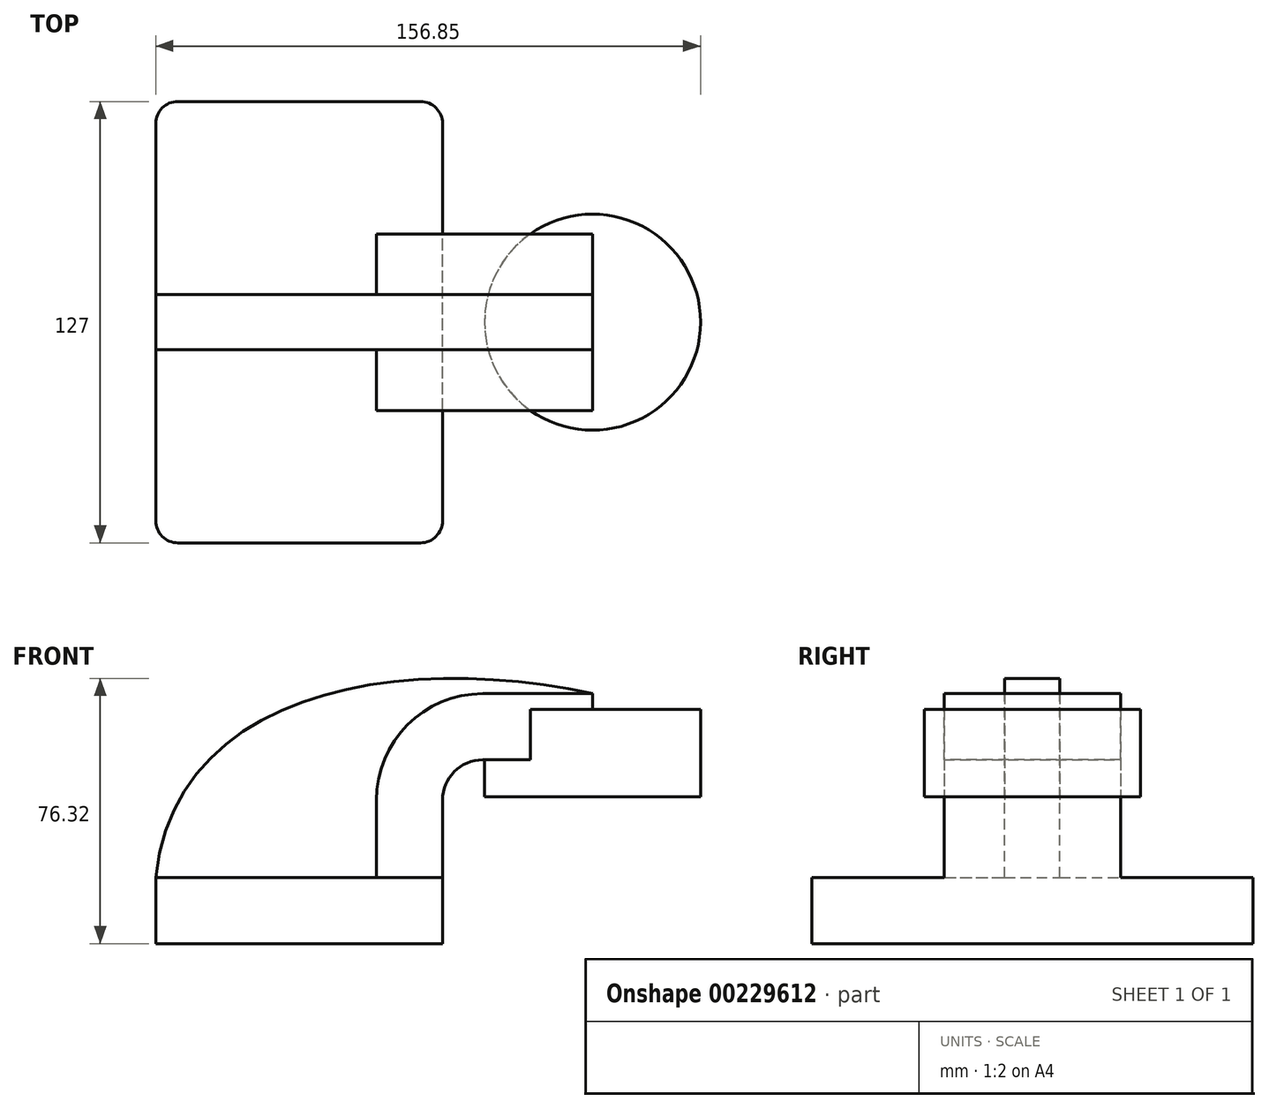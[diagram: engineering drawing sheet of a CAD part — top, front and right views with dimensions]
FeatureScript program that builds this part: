
annotation { "Feature Type Name" : "Feature", "Feature Type Description" : "" }
export const myFeature = defineFeature(function(context is Context, id is Id, definition is map)
    precondition{}
    {
        {
            var Q0;
            Q0=qCreatedBy(makeId("Front.planeOp"),FACE);
            var sketch = newSketch(context, id + "F0", { "sketchPlane" : qUnion([Q0])});
            skLineSegment(sketch, "E0.bottom", {"start": v(-41.28, -9.53) * mm, "end": v(41.28, -9.53) * mm});
            skLineSegment(sketch, "E0.top", {"start": v(-41.28, 9.52) * mm, "end": v(41.28, 9.52) * mm});
            skLineSegment(sketch, "E0.left", {"start": v(-41.28, -9.53) * mm, "end": v(-41.28, 9.53) * mm});
            skLineSegment(sketch, "E0.right", {"start": v(41.28, -9.53) * mm, "end": v(41.28, 9.52) * mm});
            skPoint(sketch, "E0.middle", {"position": v(0, 0) * mm});
            skLineSegment(sketch, "E1.bottom", {"start": v(64.77, 32.69) * mm, "end": v(115.57, 32.69) * mm});
            skLineSegment(sketch, "E1.top", {"start": v(64.77, 57.83) * mm, "end": v(115.57, 57.83) * mm});
            skLineSegment(sketch, "E1.left", {"start": v(64.77, 32.69) * mm, "end": v(64.77, 57.83) * mm});
            skLineSegment(sketch, "E1.right", {"start": v(115.57, 32.69) * mm, "end": v(115.57, 57.83) * mm});
            skPoint(sketch, "E1.middle", {"position": v(90.17, 45.26) * mm});
            skLineSegment(sketch, "E2", {"start": v(41.28, 9.52) * mm, "end": v(41.28, 31.75) * mm});
            skArc(sketch, "E3", {"start": v(41.27, 31.75) * mm, "mid": v(44.67, 39.94) * mm, "end": v(52.86, 43.33) * mm});
            skLineSegment(sketch, "E4", {"start": v(52.86, 43.33) * mm, "end": v(84.48, 43.33) * mm});
            skLineSegment(sketch, "E5.0", {"start": v(52.86, 62.38) * mm, "end": v(84.48, 62.38) * mm});
            skArc(sketch, "E5.1", {"start": v(22.22, 31.75) * mm, "mid": v(31.2, 53.41) * mm, "end": v(52.86, 62.38) * mm});
            skLineSegment(sketch, "E5.2", {"start": v(22.22, 9.52) * mm, "end": v(22.22, 31.75) * mm});
            skLineSegment(sketch, "E6", {"start": v(84.48, 62.38) * mm, "end": v(84.48, 32.69) * mm});
            skFitSpline(sketch, "E7", {"points": [v(-41.28, 9.52) * mm, v(84.48, 62.38) * mm], "startDerivative": vector(17.59, 165.45) * mm, "endDerivative": vector(159, -34.92) * mm});
            skSolve(sketch);
        }
        {
            var Q0;
            Q0=makeQuery(id+"F0.imprint","IMPRINT",FACE,{"disambiguationData":[TD([[makeQuery(id+"F0.imprint","IMPRINT",EDGE,{"derivedFrom":sQuery(id+"F0.wireOp",EDGE,"E0.bottom")}),1.0]])]});
            extrude(context, id + "F1", {"entities" : qUnion([Q0]), "depth" : 127 * mm, "symmetric" : true});
        }
        {
            var Q0;
            {var subQ0=sQuery(id+"F0.wireOp",EDGE,"E2");Q0=makeQuery(id+"F0.imprint","IMPRINT",FACE,{"disambiguationData":[TD([[makeQuery(id+"F0.imprint","IMPRINT",EDGE,{"derivedFrom":subQ0}),1.0]])]});}
            var Q1;
            {var subQ0=sQuery(id+"F0.wireOp",EDGE,"E1.left");var subQ1=sQuery(id+"F0.wireOp",EDGE,"E1.top");var subQ2=makeQuery(id+"F0.imprint","INTERSECT",VERTEX,{"derivedFrom":[subQ1,subQ0]});Q1=makeQuery(id+"F0.imprint","IMPRINT",FACE,{"disambiguationData":[TD([[makeQuery(id+"F0.imprint","IMPRINT",EDGE,{"disambiguationData":[TD([[subQ2,-1.0]])],"derivedFrom":subQ1}),-1.0]])]});}
            extrude(context, id + "F2", {"entities" : qUnion([Q0, Q1]), "operationType" : NewBodyOperationType.ADD, "depth" : 50.8 * mm, "symmetric" : true});
        }
        {
            var Q0;
            Q0=makeQuery(id+"F0.imprint","IMPRINT",FACE,{"disambiguationData":[TD([[makeQuery(id+"F0.imprint","IMPRINT",EDGE,{"derivedFrom":sQuery(id+"F0.wireOp",EDGE,"E5.0")}),1.0]])]});
            extrude(context, id + "F3", {"entities" : qUnion([Q0]), "operationType" : NewBodyOperationType.ADD, "depth" : 15.88 * mm, "symmetric" : true});
        }
        {
            var Q0;
            {var subQ0=sQuery(id+"F0.wireOp",EDGE,"E1.right");Q0=makeQuery(id+"F0.imprint","IMPRINT",FACE,{"disambiguationData":[TD([[makeQuery(id+"F0.imprint","IMPRINT",EDGE,{"derivedFrom":subQ0}),1.0]])]});}
            var Q1;
            Q1=sQuery(id+"F0.wireOp",EDGE,"E6");
            revolve(context, id + "F4", {"operationType" : NewBodyOperationType.ADD, "entities" : qUnion([Q0]), "axis" : qUnion([Q1]), "revolveType" : RevolveType.FULL});
        }
        {
            var Q0;
            Q0=makeQuery(id+"F1.opExtrude","CAP_EDGE",EDGE,{"disambiguationData":[OSD([sQuery(id+"F0.wireOp",EDGE,"E0.right")])],"isStart":false});
            var Q1;
            Q1=makeQuery(id+"F1.opExtrude","CAP_EDGE",EDGE,{"disambiguationData":[OSD([sQuery(id+"F0.wireOp",EDGE,"E0.left")])],"isStart":false});
            var Q2;
            Q2=makeQuery(id+"F1.opExtrude","CAP_EDGE",EDGE,{"disambiguationData":[OSD([sQuery(id+"F0.wireOp",EDGE,"E0.left")])],"isStart":true});
            var Q3;
            Q3=makeQuery(id+"F1.opExtrude","CAP_EDGE",EDGE,{"disambiguationData":[OSD([sQuery(id+"F0.wireOp",EDGE,"E0.right")])],"isStart":true});
            fillet(context, id + "F5", {"entities" : qUnion([Q0, Q1, Q2, Q3]), "radius" : 6.35 * mm, "tangentPropagation" : true, "allowEdgeOverflow" : false});
        }
    });
